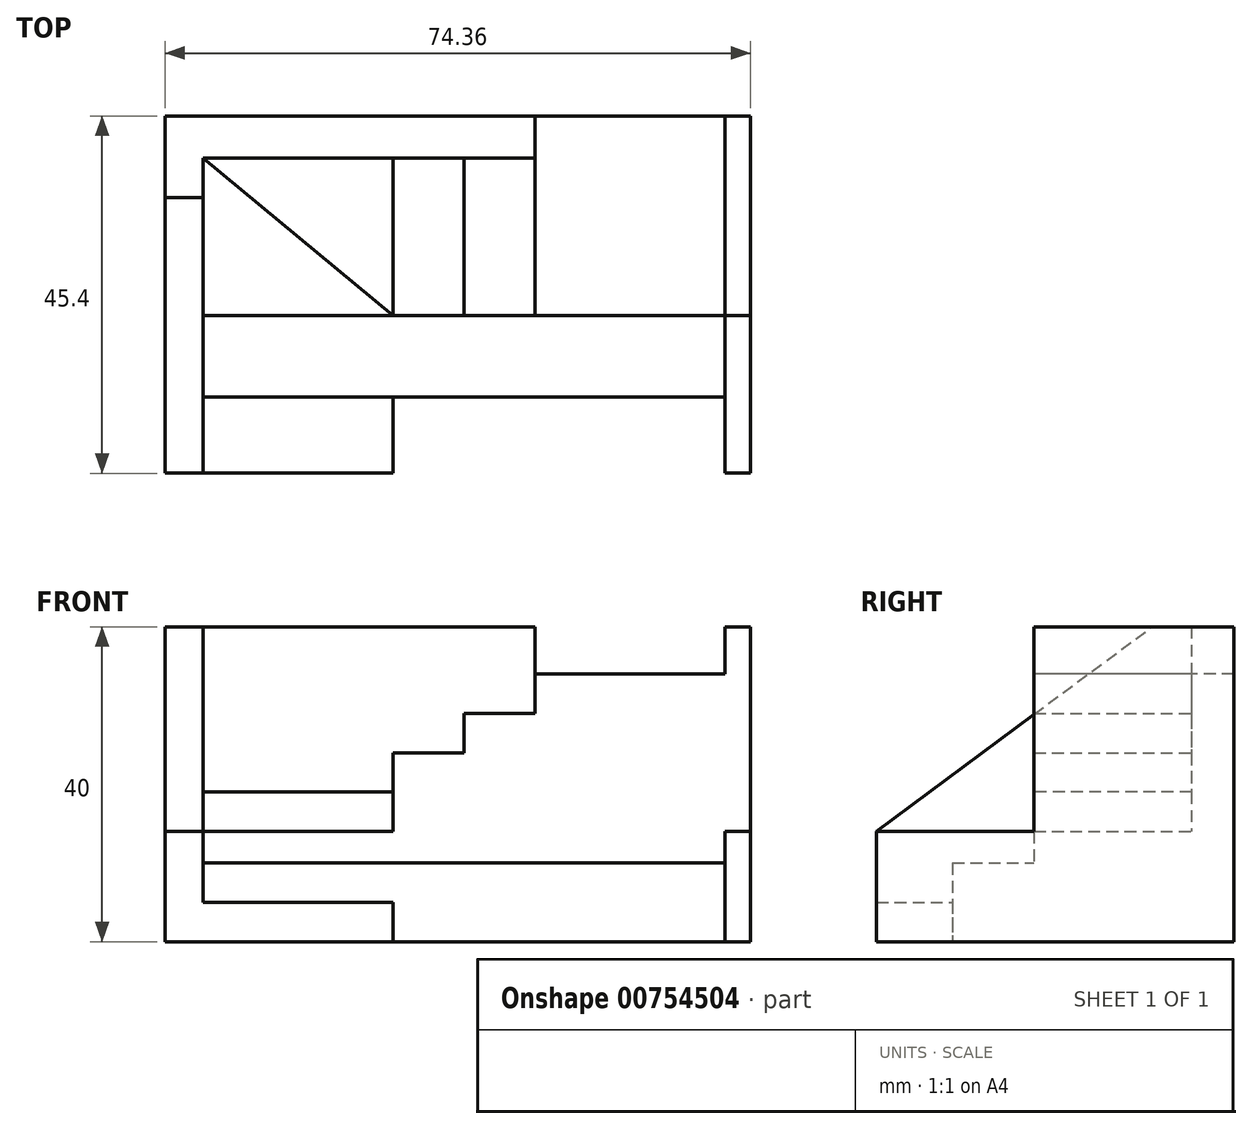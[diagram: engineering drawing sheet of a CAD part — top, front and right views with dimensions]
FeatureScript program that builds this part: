
annotation { "Feature Type Name" : "Feature", "Feature Type Description" : "" }
export const myFeature = defineFeature(function(context is Context, id is Id, definition is map)
    precondition{}
    {
        {
            var Q0;
            Q0=qCreatedBy(makeId("Top.planeOp"),FACE);
            var sketch = newSketch(context, id + "F0", { "sketchPlane" : qUnion([Q0])});
            skLineSegment(sketch, "E0.bottom", {"start": v(-37.18, -22.7) * mm, "end": v(-8.2, -22.7) * mm});
            skLineSegment(sketch, "E0.top", {"start": v(-37.18, 22.7) * mm, "end": v(37.18, 22.7) * mm});
            skLineSegment(sketch, "E0.left", {"start": v(-37.18, -22.7) * mm, "end": v(-37.18, 22.7) * mm});
            skLineSegment(sketch, "E0.right", {"start": v(37.18, -22.7) * mm, "end": v(37.18, 22.7) * mm});
            skPoint(sketch, "E0.middle", {"position": v(0, 0) * mm});
            skLineSegment(sketch, "E1", {"start": v(-32.35, -22.7) * mm, "end": v(-32.35, 17.32) * mm});
            skLineSegment(sketch, "E2", {"start": v(-32.35, -13.04) * mm, "end": v(33.94, -13.04) * mm});
            skLineSegment(sketch, "E3", {"start": v(-37.18, 17.32) * mm, "end": v(9.8, 17.32) * mm});
            skLineSegment(sketch, "E4", {"start": v(-8.2, -22.7) * mm, "end": v(-8.2, -13.04) * mm});
            skLineSegment(sketch, "E5", {"start": v(33.94, 22.7) * mm, "end": v(33.94, -22.7) * mm});
            skLineSegment(sketch, "E6.trimOffspring", {"start": v(33.94, -22.7) * mm, "end": v(37.18, -22.7) * mm});
            skLineSegment(sketch, "E7", {"start": v(-32.35, -2.69) * mm, "end": v(33.94, -2.69) * mm});
            skLineSegment(sketch, "E8", {"start": v(-8.2, -2.69) * mm, "end": v(-8.2, 17.32) * mm});
            skLineSegment(sketch, "E9", {"start": v(-32.35, 17.32) * mm, "end": v(-8.2, -2.69) * mm});
            skLineSegment(sketch, "E10", {"start": v(9.8, 22.7) * mm, "end": v(9.8, -2.69) * mm});
            skLineSegment(sketch, "E11", {"start": v(0.8, -2.69) * mm, "end": v(0.8, 17.32) * mm});
            skLineSegment(sketch, "E12", {"start": v(33.94, -2.69) * mm, "end": v(37.18, -2.69) * mm});
            skSolve(sketch);
        }
        {
            var Q0;
            {var subQ3=sQuery(id+"F0.wireOp",EDGE,"E0.bottom");var subQ5=sQuery(id+"F0.wireOp",EDGE,"E0.left");var subQ6=makeQuery(id+"F0.imprint","INTERSECT",VERTEX,{"derivedFrom":[subQ3,subQ5]});Q0=makeQuery(id+"F0.imprint","IMPRINT",FACE,{"disambiguationData":[TD([[makeQuery(id+"F0.imprint","IMPRINT",EDGE,{"disambiguationData":[TD([[subQ6,-1.0]])],"derivedFrom":subQ3}),1.0]])]});}
            extrude(context, id + "F1", {"entities" : qUnion([Q0]), "depth" : 40 * mm, "offsetDistance" : 25 * mm});
        }
        {
            var Q0;
            Q0=makeQuery(id+"F1.opExtrude","SWEPT_FACE",FACE,{"disambiguationData":[OSD([sQuery(id+"F0.wireOp",EDGE,"E1")])]});
            var sketch = newSketch(context, id + "F2", { "sketchPlane" : qUnion([Q0])});
            skLineSegment(sketch, "E13", {"start": v(-22.7, 14) * mm, "end": v(12.32, 40) * mm});
            skSolve(sketch);
        }
        {
            var Q0;
            {var subQ0=sQuery(id+"F2.wireOp",EDGE,"E13");Q0=makeQuery(id+"F2.imprint","IMPRINT",FACE,{"disambiguationData":[TD([[makeQuery(id+"F2.imprint","IMPRINT",EDGE,{"derivedFrom":subQ0}),1.0]])]});}
            extrude(context, id + "F3", {"entities" : qUnion([Q0]), "operationType" : NewBodyOperationType.REMOVE, "oppositeDirection" : true, "depth" : 25 * mm, "offsetDistance" : 25 * mm});
        }
        {
            var Q0;
            {var subQ3=sQuery(id+"F0.wireOp",EDGE,"E0.left");var subQ5=sQuery(id+"F0.wireOp",EDGE,"E0.top");var subQ6=makeQuery(id+"F0.imprint","INTERSECT",VERTEX,{"derivedFrom":[subQ5,subQ3]});Q0=makeQuery(id+"F0.imprint","IMPRINT",FACE,{"disambiguationData":[TD([[makeQuery(id+"F0.imprint","IMPRINT",EDGE,{"disambiguationData":[TD([[subQ6,-1.0]])],"derivedFrom":subQ5}),-1.0]])]});}
            extrude(context, id + "F4", {"entities" : qUnion([Q0]), "operationType" : NewBodyOperationType.ADD, "depth" : 40 * mm, "offsetDistance" : 25 * mm});
        }
        {
            var Q0;
            {var subQ0=sQuery(id+"F0.wireOp",EDGE,"E9");Q0=makeQuery(id+"F0.imprint","IMPRINT",FACE,{"disambiguationData":[TD([[makeQuery(id+"F0.imprint","IMPRINT",EDGE,{"derivedFrom":subQ0}),-1.0]])]});}
            extrude(context, id + "F5", {"entities" : qUnion([Q0]), "operationType" : NewBodyOperationType.ADD, "depth" : 14 * mm, "offsetDistance" : 25 * mm});
        }
        {
            var Q0;
            {var subQ2=sQuery(id+"F0.wireOp",EDGE,"E8");Q0=makeQuery(id+"F0.imprint","IMPRINT",FACE,{"disambiguationData":[TD([[makeQuery(id+"F0.imprint","IMPRINT",EDGE,{"derivedFrom":subQ2}),1.0]])]});}
            extrude(context, id + "F6", {"entities" : qUnion([Q0]), "operationType" : NewBodyOperationType.ADD, "depth" : 19 * mm, "offsetDistance" : 25 * mm});
        }
        {
            var Q0;
            {var subQ0=sQuery(id+"F0.wireOp",EDGE,"E8");Q0=makeQuery(id+"F0.imprint","IMPRINT",FACE,{"disambiguationData":[TD([[makeQuery(id+"F0.imprint","IMPRINT",EDGE,{"derivedFrom":subQ0}),-1.0]])]});}
            extrude(context, id + "F7", {"entities" : qUnion([Q0]), "operationType" : NewBodyOperationType.ADD, "depth" : 24 * mm, "offsetDistance" : 25 * mm});
        }
        {
            var Q0;
            {var subQ3=sQuery(id+"F0.wireOp",EDGE,"E11");Q0=makeQuery(id+"F0.imprint","IMPRINT",FACE,{"disambiguationData":[TD([[makeQuery(id+"F0.imprint","IMPRINT",EDGE,{"derivedFrom":subQ3}),-1.0]])]});}
            extrude(context, id + "F8", {"entities" : qUnion([Q0]), "operationType" : NewBodyOperationType.ADD, "depth" : 29 * mm, "offsetDistance" : 25 * mm});
        }
        {
            var Q0;
            {var subQ1=sQuery(id+"F0.wireOp",EDGE,"E5");var subQ5=sQuery(id+"F0.wireOp",EDGE,"E0.top");var subQ6=makeQuery(id+"F0.imprint","INTERSECT",VERTEX,{"derivedFrom":[subQ5,subQ1]});Q0=makeQuery(id+"F0.imprint","IMPRINT",FACE,{"disambiguationData":[TD([[makeQuery(id+"F0.imprint","IMPRINT",EDGE,{"disambiguationData":[TD([[subQ6,1.0]])],"derivedFrom":subQ5}),-1.0]])]});}
            extrude(context, id + "F9", {"entities" : qUnion([Q0]), "operationType" : NewBodyOperationType.ADD, "depth" : 34 * mm, "offsetDistance" : 25 * mm});
        }
        {
            var Q0;
            {var subQ1=sQuery(id+"F0.wireOp",EDGE,"E2");var subQ7=sQuery(id+"F0.wireOp",EDGE,"E1");var subQ8=makeQuery(id+"F0.imprint","INTERSECT",VERTEX,{"derivedFrom":[subQ7,subQ1]});Q0=makeQuery(id+"F0.imprint","IMPRINT",FACE,{"disambiguationData":[TD([[makeQuery(id+"F0.imprint","IMPRINT",EDGE,{"disambiguationData":[TD([[subQ8,-1.0]])],"derivedFrom":subQ7}),-1.0]])]});}
            extrude(context, id + "F10", {"entities" : qUnion([Q0]), "operationType" : NewBodyOperationType.ADD, "depth" : 10 * mm, "offsetDistance" : 25 * mm});
        }
        {
            var Q0;
            {var subQ0=sQuery(id+"F0.wireOp",EDGE,"E4");Q0=makeQuery(id+"F0.imprint","IMPRINT",FACE,{"disambiguationData":[TD([[makeQuery(id+"F0.imprint","IMPRINT",EDGE,{"derivedFrom":subQ0}),1.0]])]});}
            extrude(context, id + "F11", {"entities" : qUnion([Q0]), "operationType" : NewBodyOperationType.ADD, "depth" : 5 * mm, "offsetDistance" : 25 * mm});
        }
        {
            var Q0;
            {var subQ5=sQuery(id+"F0.wireOp",EDGE,"E12");Q0=makeQuery(id+"F0.imprint","IMPRINT",FACE,{"disambiguationData":[TD([[makeQuery(id+"F0.imprint","IMPRINT",EDGE,{"derivedFrom":subQ5}),1.0]])]});}
            extrude(context, id + "F12", {"entities" : qUnion([Q0]), "operationType" : NewBodyOperationType.ADD, "depth" : 40 * mm, "offsetDistance" : 25 * mm});
        }
        {
            var Q0;
            {var subQ2=sQuery(id+"F0.wireOp",EDGE,"E6.trimOffspring");Q0=makeQuery(id+"F0.imprint","IMPRINT",FACE,{"disambiguationData":[TD([[makeQuery(id+"F0.imprint","IMPRINT",EDGE,{"derivedFrom":subQ2}),1.0]])]});}
            extrude(context, id + "F13", {"entities" : qUnion([Q0]), "operationType" : NewBodyOperationType.ADD, "depth" : 14 * mm, "offsetDistance" : 25 * mm});
        }
    });
